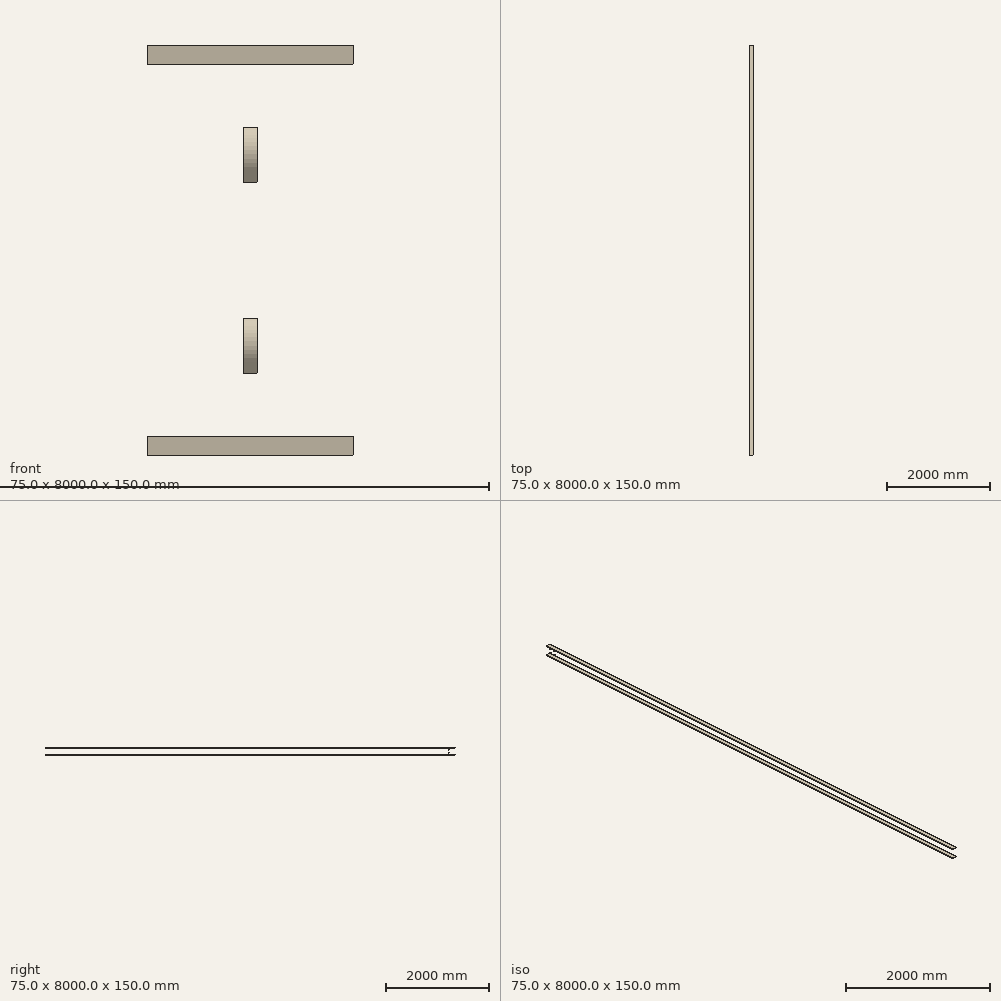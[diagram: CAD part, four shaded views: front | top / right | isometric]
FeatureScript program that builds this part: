
annotation { "Feature Type Name" : "Feature", "Feature Type Description" : "" }
export const myFeature = defineFeature(function(context is Context, id is Id, definition is map)
    precondition{}
    {
        {
            var Q0;
            Q0=qCreatedBy(makeId("Front.planeOp"),FACE);
            var sketch = newSketch(context, id + "F0", { "sketchPlane" : qUnion([Q0])});
            skLineSegment(sketch, "E0", {"start": v(0, 75) * mm, "end": v(37.5, 75) * mm});
            skLineSegment(sketch, "E1", {"start": v(37.5, 75) * mm, "end": v(37.5, 68) * mm});
            skLineSegment(sketch, "E2", {"start": v(37.5, 68) * mm, "end": v(2.5, 68) * mm});
            skLineSegment(sketch, "E3", {"start": v(2.5, 68) * mm, "end": v(2.5, -68) * mm});
            skLineSegment(sketch, "E4", {"start": v(2.5, -68) * mm, "end": v(37.5, -68) * mm});
            skLineSegment(sketch, "E5", {"start": v(37.5, -68) * mm, "end": v(37.5, -75) * mm});
            skLineSegment(sketch, "E6", {"start": v(37.5, -75) * mm, "end": v(0, -75) * mm});
            skLineSegment(sketch, "E7.MirrorCS", {"start": v(0, 75) * mm, "end": v(-37.5, 75) * mm});
            skLineSegment(sketch, "E8.MirrorCS", {"start": v(-37.5, 75) * mm, "end": v(-37.5, 68) * mm});
            skLineSegment(sketch, "E9.MirrorCS", {"start": v(-37.5, 68) * mm, "end": v(-2.5, 68) * mm});
            skLineSegment(sketch, "E10.MirrorCS", {"start": v(-2.5, 68) * mm, "end": v(-2.5, -68) * mm});
            skLineSegment(sketch, "E11.MirrorCS", {"start": v(-2.5, -68) * mm, "end": v(-37.5, -68) * mm});
            skLineSegment(sketch, "E12.MirrorCS", {"start": v(-37.5, -68) * mm, "end": v(-37.5, -75) * mm});
            skLineSegment(sketch, "E13.MirrorCS", {"start": v(-37.5, -75) * mm, "end": v(0, -75) * mm});
            skSolve(sketch);
        }
        {
            var Q0;
            Q0 = qSketchRegion(id + "F0", true);
            extrude(context, id + "F1", {"entities" : qUnion([Q0]), "endBound" : BoundingType.SYMMETRIC, "depth" : 8000 * mm});
        }
        {
            var Q0;
            Q0=makeQuery(id+"F1.opExtrude","SWEPT_FACE",FACE,{"disambiguationData":[OSD([sQuery(id+"F0.wireOp",EDGE,"E3")])]});
            var sketch = newSketch(context, id + "F2", { "sketchPlane" : qUnion([Q0])});
            skCircle(sketch, "E14", {"center": v(-3960, 35) * mm, "radius": 10 * mm});
            skCircle(sketch, "E15", {"center": v(-3960, -35) * mm, "radius": 10 * mm});
            skLineSegment(sketch, "E16", {"start": v(0, 68) * mm, "end": v(0, -68) * mm, "construction": true});
            skCircle(sketch, "E17.MirrorC", {"center": v(3960, 35) * mm, "radius": 10 * mm});
            skCircle(sketch, "E18.MirrorC", {"center": v(3960, -35) * mm, "radius": 10 * mm});
            skCircle(sketch, "E19", {"center": v(-3880, 35) * mm, "radius": 10 * mm});
            skCircle(sketch, "E20", {"center": v(-3880, -35) * mm, "radius": 10 * mm});
            skCircle(sketch, "E21.MirrorC", {"center": v(3880, 35) * mm, "radius": 10 * mm});
            skCircle(sketch, "E22.MirrorC", {"center": v(3880, -35) * mm, "radius": 10 * mm});
            skSolve(sketch);
        }
        {
            var Q0;
            Q0=makeQuery(id+"F2.imprint","IMPRINT",FACE,{"disambiguationData":[TD([[makeQuery(id+"F2.imprint","IMPRINT",EDGE,{"derivedFrom":sQuery(id+"F2.wireOp",EDGE,"E14")}),1.0]])]});
            var Q1;
            Q1=makeQuery(id+"F2.imprint","IMPRINT",FACE,{"disambiguationData":[TD([[makeQuery(id+"F2.imprint","IMPRINT",EDGE,{"derivedFrom":sQuery(id+"F2.wireOp",EDGE,"E15")}),1.0]])]});
            var Q2;
            Q2=makeQuery(id+"F2.imprint","IMPRINT",FACE,{"disambiguationData":[TD([[makeQuery(id+"F2.imprint","IMPRINT",EDGE,{"derivedFrom":sQuery(id+"F2.wireOp",EDGE,"E17.MirrorC")}),-1.0]])]});
            var Q3;
            Q3=makeQuery(id+"F2.imprint","IMPRINT",FACE,{"disambiguationData":[TD([[makeQuery(id+"F2.imprint","IMPRINT",EDGE,{"derivedFrom":sQuery(id+"F2.wireOp",EDGE,"E18.MirrorC")}),-1.0]])]});
            var Q4;
            Q4=makeQuery(id+"F2.imprint","IMPRINT",FACE,{"disambiguationData":[TD([[makeQuery(id+"F2.imprint","IMPRINT",EDGE,{"derivedFrom":sQuery(id+"F2.wireOp",EDGE,"E19")}),1.0]])]});
            var Q5;
            Q5=makeQuery(id+"F2.imprint","IMPRINT",FACE,{"disambiguationData":[TD([[makeQuery(id+"F2.imprint","IMPRINT",EDGE,{"derivedFrom":sQuery(id+"F2.wireOp",EDGE,"E20")}),1.0]])]});
            var Q6;
            Q6=makeQuery(id+"F2.imprint","IMPRINT",FACE,{"disambiguationData":[TD([[makeQuery(id+"F2.imprint","IMPRINT",EDGE,{"derivedFrom":sQuery(id+"F2.wireOp",EDGE,"E21.MirrorC")}),-1.0]])]});
            var Q7;
            Q7=makeQuery(id+"F2.imprint","IMPRINT",FACE,{"disambiguationData":[TD([[makeQuery(id+"F2.imprint","IMPRINT",EDGE,{"derivedFrom":sQuery(id+"F2.wireOp",EDGE,"E22.MirrorC")}),-1.0]])]});
            extrude(context, id + "F3", {"entities" : qUnion([Q0, Q1, Q2, Q3, Q4, Q5, Q6, Q7]), "operationType" : NewBodyOperationType.REMOVE, "endBound" : BoundingType.THROUGH_ALL, "oppositeDirection" : true, "depth" : 25 * mm});
        }
    });
